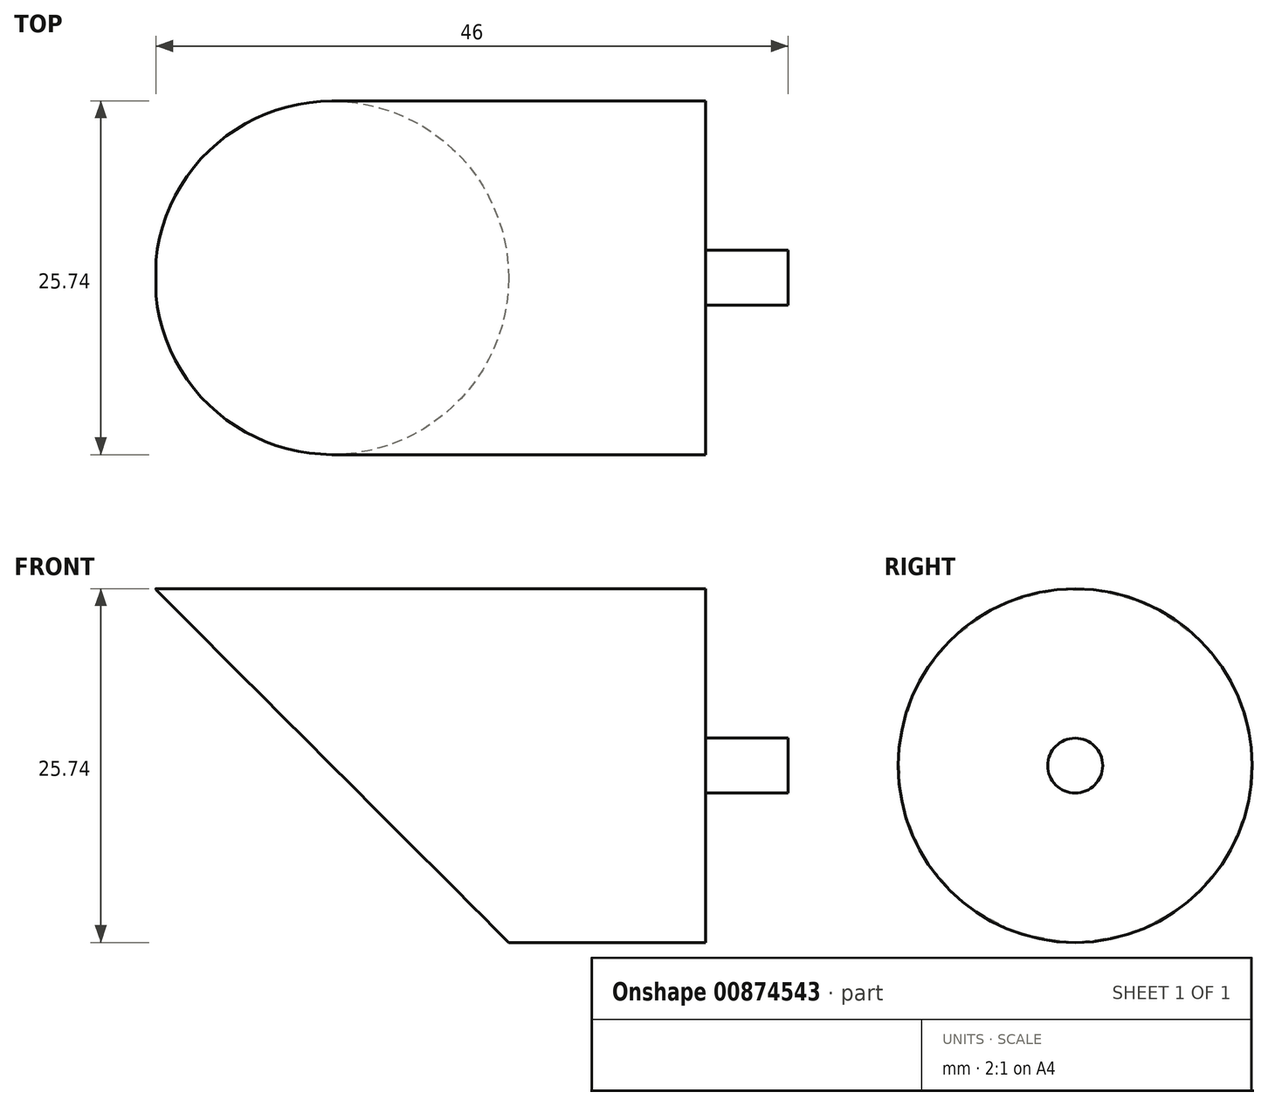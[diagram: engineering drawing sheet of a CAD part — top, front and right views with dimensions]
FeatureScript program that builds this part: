
annotation { "Feature Type Name" : "Feature", "Feature Type Description" : "" }
export const myFeature = defineFeature(function(context is Context, id is Id, definition is map)
    precondition{}
    {
        {
            var Q0;
            Q0=qCreatedBy(makeId("Right.planeOp"),FACE);
            var sketch = newSketch(context, id + "F0", { "sketchPlane" : qUnion([Q0])});
            skCircle(sketch, "E0", {"center": v(0, 0) * mm, "radius": 12.87 * mm});
            skSolve(sketch);
        }
        {
            var Q0;
            Q0=makeQuery(id+"F0.imprint","IMPRINT",FACE,{"disambiguationData":[TD([[makeQuery(id+"F0.imprint","IMPRINT",EDGE,{"derivedFrom":sQuery(id+"F0.wireOp",EDGE,"E0")}),1.0]])]});
            var Q1;
            Q1=sQuery(id+"F0.wireOp",EDGE,"E0");
            extrude(context, id + "F1", {"entities" : qUnion([Q0]), "surfaceEntities" : qUnion([Q1]), "oppositeDirection" : true, "depth" : 40 * mm, "offsetDistance" : 25 * mm});
        }
        {
            var Q0;
            Q0=qCreatedBy(makeId("Front.planeOp"),FACE);
            var sketch = newSketch(context, id + "F2", { "sketchPlane" : qUnion([Q0])});
            skLineSegment(sketch, "E1", {"start": v(-40.08, 12.89) * mm, "end": v(-40.08, -13.17) * mm});
            skLineSegment(sketch, "E2", {"start": v(-40.08, -13.17) * mm, "end": v(-14.02, -13.17) * mm});
            skLineSegment(sketch, "E3", {"start": v(-14.02, -13.17) * mm, "end": v(-40.08, 12.89) * mm});
            skSolve(sketch);
        }
        {
            var Q0;
            Q0=makeQuery(id+"F2.imprint","IMPRINT",FACE,{"disambiguationData":[TD([[makeQuery(id+"F2.imprint","IMPRINT",EDGE,{"derivedFrom":sQuery(id+"F2.wireOp",EDGE,"E1")}),1.0]])]});
            extrude(context, id + "F3", {"entities" : qUnion([Q0]), "operationType" : NewBodyOperationType.REMOVE, "endBound" : BoundingType.SYMMETRIC, "depth" : 30 * mm, "offsetDistance" : 25 * mm});
        }
        {
            var Q0;
            Q0=makeQuery(id+"F1.opExtrude","CAP_FACE",FACE,{"disambiguationData":[OSD([sQuery(id+"F0.wireOp",EDGE,"E0")])],"isStart":true});
            var sketch = newSketch(context, id + "F4", { "sketchPlane" : qUnion([Q0])});
            skCircle(sketch, "E4", {"center": v(0, 0) * mm, "radius": 2 * mm});
            skSolve(sketch);
        }
        {
            var Q0;
            Q0=makeQuery(id+"F4.imprint","IMPRINT",FACE,{"disambiguationData":[TD([[makeQuery(id+"F4.imprint","IMPRINT",EDGE,{"derivedFrom":sQuery(id+"F4.wireOp",EDGE,"E4")}),1.0]])]});
            extrude(context, id + "F5", {"entities" : qUnion([Q0]), "operationType" : NewBodyOperationType.ADD, "depth" : 6 * mm, "offsetDistance" : 25 * mm});
        }
    });
